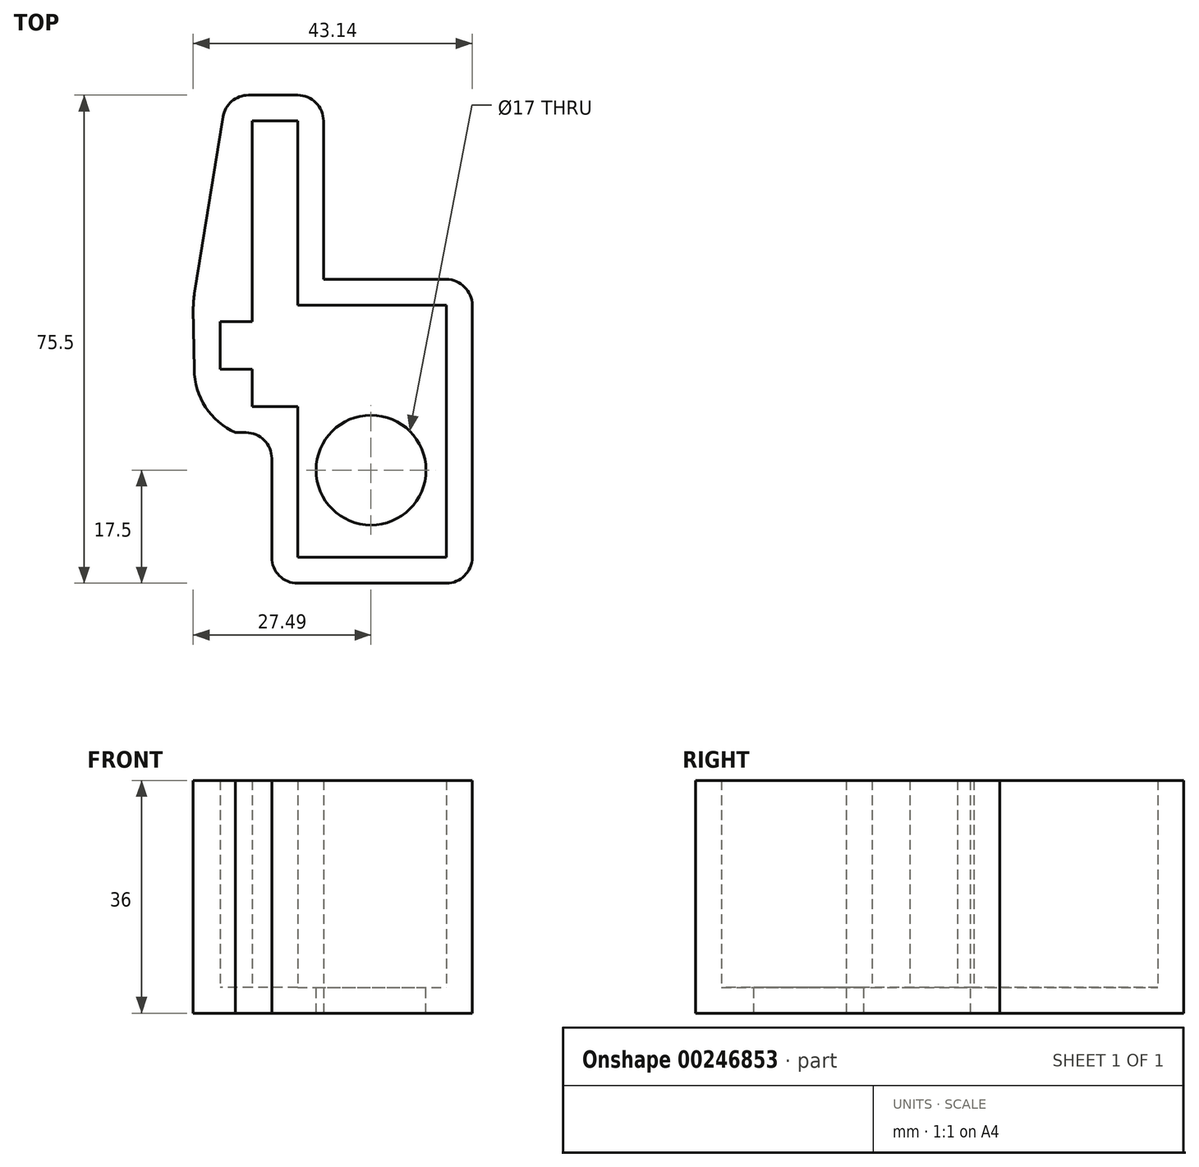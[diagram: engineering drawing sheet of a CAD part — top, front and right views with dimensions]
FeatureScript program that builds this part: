
annotation { "Feature Type Name" : "Feature", "Feature Type Description" : "" }
export const myFeature = defineFeature(function(context is Context, id is Id, definition is map)
    precondition{}
    {
        {
            var Q0;
            Q0=qCreatedBy(makeId("Top.planeOp"),FACE);
            var sketch = newSketch(context, id + "F0", { "sketchPlane" : qUnion([Q0])});
            skLineSegment(sketch, "E0", {"start": v(0, 0) * mm, "end": v(-7, 0) * mm});
            skLineSegment(sketch, "E1", {"start": v(-7, 0) * mm, "end": v(-7, 5.8) * mm});
            skLineSegment(sketch, "E2", {"start": v(-7, 5.8) * mm, "end": v(-12, 5.8) * mm});
            skLineSegment(sketch, "E3", {"start": v(-12, 5.8) * mm, "end": v(-12, 13.2) * mm});
            skLineSegment(sketch, "E4", {"start": v(-12, 13.2) * mm, "end": v(-7, 13.2) * mm});
            skLineSegment(sketch, "E5", {"start": v(-7, 13.2) * mm, "end": v(-7, 44.2) * mm});
            skLineSegment(sketch, "E6", {"start": v(-7, 44.2) * mm, "end": v(0, 44.2) * mm});
            skLineSegment(sketch, "E7", {"start": v(0, 44.2) * mm, "end": v(0, 15.7) * mm});
            skLineSegment(sketch, "E8", {"start": v(0, 15.7) * mm, "end": v(23, 15.7) * mm});
            skLineSegment(sketch, "E9", {"start": v(23, 15.7) * mm, "end": v(23, -23.3) * mm});
            skLineSegment(sketch, "E10", {"start": v(23, -23.3) * mm, "end": v(0, -23.3) * mm});
            skLineSegment(sketch, "E11", {"start": v(0, -23.3) * mm, "end": v(0, 0) * mm});
            skLineSegment(sketch, "E12", {"start": v(23, -23.3) * mm, "end": v(23, -27.3) * mm, "construction": true});
            skLineSegment(sketch, "E13", {"start": v(23, -27.3) * mm, "end": v(0, -27.3) * mm});
            skLineSegment(sketch, "E14", {"start": v(0, -27.3) * mm, "end": v(0, -27.3) * mm});
            skLineSegment(sketch, "E15", {"start": v(-4, -8) * mm, "end": v(-4, -23.3) * mm});
            skLineSegment(sketch, "E16", {"start": v(0, 0) * mm, "end": v(0, -4) * mm, "construction": true});
            skLineSegment(sketch, "E17", {"start": v(0, -4) * mm, "end": v(-4, -4) * mm, "construction": true});
            skPoint(sketch, "E18.orphan", {"position": v(-4, 0) * mm});
            skLineSegment(sketch, "E19", {"start": v(-4, -23.3) * mm, "end": v(-4, -23.3) * mm});
            skLineSegment(sketch, "E20", {"start": v(-7, 0) * mm, "end": v(-7, -4) * mm, "construction": true});
            skLineSegment(sketch, "E21", {"start": v(-12, 5.8) * mm, "end": v(-16, 5.8) * mm, "construction": true});
            skLineSegment(sketch, "E22", {"start": v(-12, 13.2) * mm, "end": v(-16, 13.2) * mm, "construction": true});
            skLineSegment(sketch, "E23", {"start": v(-7, 44.2) * mm, "end": v(-11, 44.2) * mm, "construction": true});
            skLineSegment(sketch, "E24", {"start": v(-7, 44.2) * mm, "end": v(-7, 48.2) * mm, "construction": true});
            skLineSegment(sketch, "E25", {"start": v(0, 44.2) * mm, "end": v(0, 48.2) * mm, "construction": true});
            skLineSegment(sketch, "E26", {"start": v(0, 44.2) * mm, "end": v(4, 44.2) * mm, "construction": true});
            skLineSegment(sketch, "E27", {"start": v(23, 15.7) * mm, "end": v(23, 19.7) * mm, "construction": true});
            skLineSegment(sketch, "E28", {"start": v(23, 15.7) * mm, "end": v(27, 15.7) * mm, "construction": true});
            skLineSegment(sketch, "E29", {"start": v(23, -23.3) * mm, "end": v(27, -23.3) * mm, "construction": true});
            skLineSegment(sketch, "E30", {"start": v(-8, -4) * mm, "end": v(-9.6, -4) * mm});
            skLineSegment(sketch, "E31", {"start": v(-16.1, 16.34) * mm, "end": v(-16.14, 16.33) * mm});
            skLineSegment(sketch, "E32", {"start": v(0, 48.2) * mm, "end": v(-7, 48.2) * mm});
            skLineSegment(sketch, "E33", {"start": v(0, 48.2) * mm, "end": v(0, 48.2) * mm});
            skLineSegment(sketch, "E34", {"start": v(4, 44.2) * mm, "end": v(4, 19.7) * mm});
            skLineSegment(sketch, "E35", {"start": v(4, 44.2) * mm, "end": v(4, 44.2) * mm});
            skLineSegment(sketch, "E36", {"start": v(23, 19.7) * mm, "end": v(4, 19.7) * mm});
            skLineSegment(sketch, "E37", {"start": v(27, 15.7) * mm, "end": v(27, 15.7) * mm});
            skLineSegment(sketch, "E38", {"start": v(-11, 43.7) * mm, "end": v(-11, 44.2) * mm});
            skLineSegment(sketch, "E39", {"start": v(23, 19.7) * mm, "end": v(23, 19.7) * mm});
            skLineSegment(sketch, "E40", {"start": v(27, 15.7) * mm, "end": v(27, -23.3) * mm});
            skLineSegment(sketch, "E41", {"start": v(23, -27.3) * mm, "end": v(23, -27.3) * mm});
            skPoint(sketch, "E42.visualSharp", {"position": v(27, 19.7) * mm});
            skArc(sketch, "E42.filletArc", {"start": v(27, 15.7) * mm, "mid": v(25.83, 18.53) * mm, "end": v(23, 19.7) * mm});
            skPoint(sketch, "E43.visualSharp", {"position": v(27, -27.3) * mm});
            skArc(sketch, "E43.filletArc", {"start": v(23, -27.3) * mm, "mid": v(25.83, -26.13) * mm, "end": v(27, -23.3) * mm});
            skPoint(sketch, "E44.visualSharp", {"position": v(-4, -27.3) * mm});
            skArc(sketch, "E44.filletArc", {"start": v(-4, -23.3) * mm, "mid": v(-2.83, -26.13) * mm, "end": v(0, -27.3) * mm});
            skPoint(sketch, "E45.visualSharp", {"position": v(-4, -4) * mm});
            skArc(sketch, "E45.filletArc", {"start": v(-4, -8) * mm, "mid": v(-5.17, -5.17) * mm, "end": v(-8, -4) * mm});
            skPoint(sketch, "E46.visualSharp", {"position": v(4, 48.2) * mm});
            skArc(sketch, "E46.filletArc", {"start": v(4, 44.2) * mm, "mid": v(2.83, 47.03) * mm, "end": v(0, 48.2) * mm});
            skPoint(sketch, "E47.visualSharp", {"position": v(-11, 48.2) * mm});
            skLineSegment(sketch, "E48", {"start": v(-7, 48.2) * mm, "end": v(-7.6, 48.2) * mm});
            skLineSegment(sketch, "E49", {"start": v(-11.54, 44.84) * mm, "end": v(-15.95, 17.52) * mm});
            skArc(sketch, "E50.filletArc", {"start": v(-7.6, 48.2) * mm, "mid": v(-10.19, 47.25) * mm, "end": v(-11.54, 44.84) * mm});
            skPoint(sketch, "E51.visualSharp", {"position": v(-16.14, 16.33) * mm});
            skArc(sketch, "E51.filletArc", {"start": v(-15.95, 17.52) * mm, "mid": v(-16.1, 16.33) * mm, "end": v(-16.14, 15.13) * mm});
            skArc(sketch, "E52", {"start": v(-16, 5.8) * mm, "mid": v(-14.23, -0.04) * mm, "end": v(-9.6, -4) * mm});
            skLineSegment(sketch, "E53", {"start": v(-16.14, 15.13) * mm, "end": v(-16, 5.8) * mm});
            skSolve(sketch);
        }
        {
            var Q0;
            Q0=makeQuery(id+"F0.imprint","IMPRINT",FACE,{"disambiguationData":[TD([[makeQuery(id+"F0.imprint","IMPRINT",EDGE,{"derivedFrom":sQuery(id+"F0.wireOp",EDGE,"E0")}),1.0]])]});
            extrude(context, id + "F1", {"entities" : qUnion([Q0]), "depth" : 32 * mm});
        }
        {
            var Q0;
            Q0=makeQuery(id+"F1.opExtrude","CAP_FACE",FACE,{"disambiguationData":[OSD([sQuery(id+"F0.wireOp",EDGE,"E0"),sQuery(id+"F0.wireOp",EDGE,"E1"),sQuery(id+"F0.wireOp",EDGE,"E2"),sQuery(id+"F0.wireOp",EDGE,"E3"),sQuery(id+"F0.wireOp",EDGE,"E4"),sQuery(id+"F0.wireOp",EDGE,"E5"),sQuery(id+"F0.wireOp",EDGE,"E6"),sQuery(id+"F0.wireOp",EDGE,"E7"),sQuery(id+"F0.wireOp",EDGE,"E8"),sQuery(id+"F0.wireOp",EDGE,"E9"),sQuery(id+"F0.wireOp",EDGE,"E10"),sQuery(id+"F0.wireOp",EDGE,"E11"),sQuery(id+"F0.wireOp",EDGE,"E13"),sQuery(id+"F0.wireOp",EDGE,"E15"),sQuery(id+"F0.wireOp",EDGE,"E30"),sQuery(id+"F0.wireOp",EDGE,"E32"),sQuery(id+"F0.wireOp",EDGE,"E34"),sQuery(id+"F0.wireOp",EDGE,"E36"),sQuery(id+"F0.wireOp",EDGE,"E40"),sQuery(id+"F0.wireOp",EDGE,"E42.filletArc"),sQuery(id+"F0.wireOp",EDGE,"E43.filletArc"),sQuery(id+"F0.wireOp",EDGE,"E44.filletArc"),sQuery(id+"F0.wireOp",EDGE,"E45.filletArc"),sQuery(id+"F0.wireOp",EDGE,"E46.filletArc"),sQuery(id+"F0.wireOp",EDGE,"E48"),sQuery(id+"F0.wireOp",EDGE,"E49"),sQuery(id+"F0.wireOp",EDGE,"E50.filletArc"),sQuery(id+"F0.wireOp",EDGE,"E51.filletArc"),sQuery(id+"F0.wireOp",EDGE,"E52"),sQuery(id+"F0.wireOp",EDGE,"E53")])],"isStart":true});
            var sketch = newSketch(context, id + "F2", { "sketchPlane" : qUnion([Q0])});
            skLineSegment(sketch, "E54.0.0", {"start": v(-7.6, -48.2) * mm, "end": v(0, -48.2) * mm});
            skArc(sketch, "E54.0.1", {"start": v(0, -48.2) * mm, "mid": v(2.83, -47.03) * mm, "end": v(4, -44.2) * mm});
            skLineSegment(sketch, "E54.0.2", {"start": v(4, -44.2) * mm, "end": v(4, -19.7) * mm});
            skLineSegment(sketch, "E54.0.3", {"start": v(4, -19.7) * mm, "end": v(23, -19.7) * mm});
            skArc(sketch, "E54.0.4", {"start": v(23, -19.7) * mm, "mid": v(25.83, -18.53) * mm, "end": v(27, -15.7) * mm});
            skLineSegment(sketch, "E54.0.5", {"start": v(27, -15.7) * mm, "end": v(27, 23.3) * mm});
            skArc(sketch, "E54.0.6", {"start": v(27, 23.3) * mm, "mid": v(25.83, 26.13) * mm, "end": v(23, 27.3) * mm});
            skLineSegment(sketch, "E54.0.7", {"start": v(23, 27.3) * mm, "end": v(0, 27.3) * mm});
            skArc(sketch, "E54.0.8", {"start": v(0, 27.3) * mm, "mid": v(-2.83, 26.13) * mm, "end": v(-4, 23.3) * mm});
            skLineSegment(sketch, "E54.0.9", {"start": v(-4, 23.3) * mm, "end": v(-4, 8) * mm});
            skArc(sketch, "E54.0.10", {"start": v(-4, 8) * mm, "mid": v(-5.17, 5.17) * mm, "end": v(-8, 4) * mm});
            skLineSegment(sketch, "E54.0.11", {"start": v(-8, 4) * mm, "end": v(-9.6, 4) * mm});
            skArc(sketch, "E54.0.12", {"start": v(-9.6, 4) * mm, "mid": v(-14.23, 0.04) * mm, "end": v(-16, -5.8) * mm});
            skLineSegment(sketch, "E54.0.13", {"start": v(-16, -5.8) * mm, "end": v(-16.14, -15.13) * mm});
            skArc(sketch, "E54.0.14", {"start": v(-16.14, -15.13) * mm, "mid": v(-16.1, -16.33) * mm, "end": v(-15.95, -17.52) * mm});
            skLineSegment(sketch, "E54.0.15", {"start": v(-15.95, -17.52) * mm, "end": v(-11.54, -44.84) * mm});
            skArc(sketch, "E54.0.16", {"start": v(-11.54, -44.84) * mm, "mid": v(-10.19, -47.25) * mm, "end": v(-7.6, -48.2) * mm});
            skLineSegment(sketch, "E55.bottom", {"start": v(0, 23.3) * mm, "end": v(11.35, 23.3) * mm, "construction": true});
            skLineSegment(sketch, "E55.top", {"start": v(0, 9.8) * mm, "end": v(11.35, 9.8) * mm, "construction": true});
            skLineSegment(sketch, "E55.left", {"start": v(0, 23.3) * mm, "end": v(0, 9.8) * mm, "construction": true});
            skLineSegment(sketch, "E55.right", {"start": v(11.35, 23.3) * mm, "end": v(11.35, 9.8) * mm, "construction": true});
            skCircle(sketch, "E56", {"center": v(11.35, 9.8) * mm, "radius": 8.5 * mm});
            skSolve(sketch);
        }
        {
            var Q0;
            Q0=makeQuery(id+"F2.imprint","IMPRINT",FACE,{"disambiguationData":[TD([[makeQuery(id+"F2.imprint","IMPRINT",EDGE,{"derivedFrom":sQuery(id+"F2.wireOp",EDGE,"E54.0.0")}),-1.0]])]});
            var Q1;
            Q1=makeQuery(id+"F2.imprint","IMPRINT",FACE,{"disambiguationData":[TD([[makeQuery(id+"F2.imprint","IMPRINT",EDGE,{"derivedFrom":sQuery(id+"F2.wireOp",EDGE,"E56")}),-1.0]])]});
            extrude(context, id + "F3", {"entities" : qUnion([Q0, Q1]), "operationType" : NewBodyOperationType.ADD, "depth" : 4 * mm});
        }
    });
